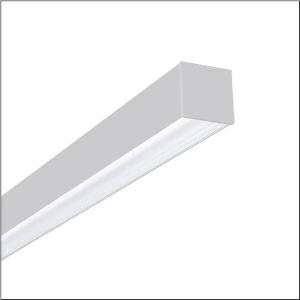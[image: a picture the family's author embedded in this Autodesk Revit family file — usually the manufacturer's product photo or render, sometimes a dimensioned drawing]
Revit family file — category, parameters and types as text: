
# Revit family: silica_r_5mx21bd1w4a_a515
name_source: partatom
category: Lighting Fixtures
units: mm (PartAtom-declared; Revit-internal decimal feet)

## family parameters
Cut with Voids When Loaded = No
Host = Face
Light Source = No
Part Type = Normal
Room Calculation Point = No
Round Connector Dimension = Use Diameter
Shared = No

## types (1)
- --- (1 x LED, 4950 lm, 29.3 W, 4000K)
    Apparent Load = 29 VA
    CIE Flux Codes = 82 97 100 100 100
    Color Rendering = 80
    Color Temperature = 4000K
    Default Elevation = 1800 mm
    Description = Silica®, office luminaire, of aluminium, light emission: direct distribution, primary light characteristic: symmetric, installation type: surface-mounted, LED, rated luminous flux: 4.950lm, luminous efficacy: 169lm/W, light colour: 840, colour temperature: 4000K, control gear: ECG DALI, with terminal, 3+2-pole, max. 2.5mm², mains connection: 230V, AC, 50/60Hz, rated input power: 29W, luminaire housing, of aluminium, traffic white (RAL 9016), length: 1.442mm, width: 65mm, height: 64mm, protection rating (complete): IP20, insulation class (complete): insulation class I (protective earthing), certification: CE, permissible operating ambient temperature: 0..+35°C, standard: EN 50419, packaging unit: 1 piece
    Height = 64 mm
    Lamp = 1 x LED
    Lamp Light Flux = 4950 lm
    Lamp Power = 29.3 W
    Lamp count = 1
    Length = 1442 mm
    Luminous efficacy = 169 lm/W
    Manufacturer = Siteco
    ModVariant = No
    Model = 5MX21BD1W4A
    Mounting Place = Ceiling
    Mounting Type = Surface mounted
    Number of Poles = 1
    OnlyDefault = Yes
    Power Factor = 1
    Product Name = Silica®
    Product group = office luminaire | ceiling mounted
    ProductGroupID = 304
    Protection Class = Protection class I
    Protection Degree = IP 20
    RLX_Detail_Level = 1
    RLX_Emergency_Light_Flux = 0 lm
    RLX_Emergency_Type = 0
    RLX_Emergency_Type_DB = No
    RlxData = <blob elided: 23397 chars, md5=7292df5c>
    Socket = socket
    Standby Power = 0 W
    System Light Flux = 4950 lm
    System Power = 29 W
    Type Comments = factory setting: luminous flux: 100 % | dim-lin: 254 | 163 mA
    Type Image = l_1003937.jpg
    URL = http://relux.com
    VarID = @adj_138596
    Voltage = 0 V
    Weight = 0.00 kg
    Width = 66 mm

## geometry (parser evidence)
native form markers: Blend x4, Sweep x13
no freeform markers — native parametric forms only
